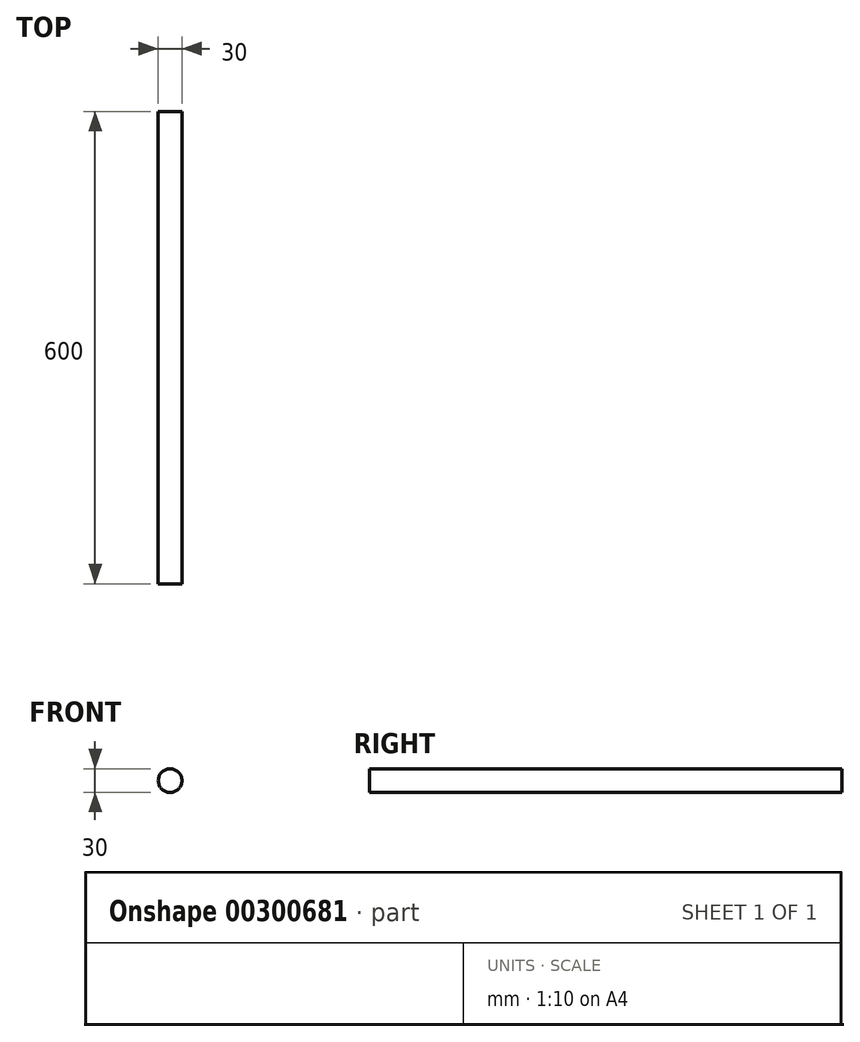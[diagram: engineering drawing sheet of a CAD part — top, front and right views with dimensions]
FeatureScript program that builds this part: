
annotation { "Feature Type Name" : "Feature", "Feature Type Description" : "" }
export const myFeature = defineFeature(function(context is Context, id is Id, definition is map)
    precondition{}
    {
        {
            var Q0;
            Q0=qCreatedBy(makeId("Front.planeOp"),FACE);
            var sketch = newSketch(context, id + "F0", { "sketchPlane" : qUnion([Q0])});
            skCircle(sketch, "E0", {"center": v(0, 0) * mm, "radius": 15 * mm});
            skSolve(sketch);
        }
        {
            var Q0;
            Q0 = qSketchRegion(id + "F0", true);
            extrude(context, id + "F1", {"entities" : qUnion([Q0]), "depth" : 600 * mm});
        }
    });
